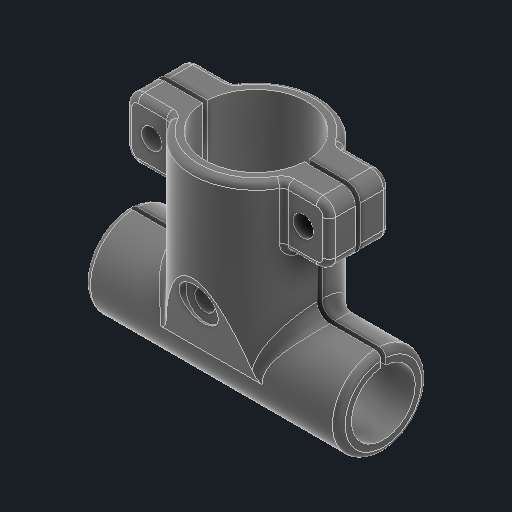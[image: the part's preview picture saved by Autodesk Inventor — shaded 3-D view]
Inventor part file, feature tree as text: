
AUTODESK INVENTOR PART (.ipt)
format: ipt  version: 2024.1 (Build 281209000, 209)  size: 550,400 bytes
history: native  units: mm
features: sketch x11, extrude x10, projected_geometry x7, fillet x4, revolve x2, plane x2
ambient origin geometry x8: Origin, YZ Plane, XZ Plane, XY Plane, X Axis, Y Axis, Z Axis, Center Point
bodies: Solid1 (feature_tree)
feature tree (36):
  sketch  "Sketch1"  dims[d0=40.0mm d1=20.0mm]
  revolve  "Revolution1"  [1 undecoded]
  revolve  "Revolution2"  [1 undecoded]
  extrude  "Extrusion1"  Depth=2.0mm
  extrude  "Extrusion2"  Depth=4.0mm
  extrude  "Extrusion3"  TaperAngle=360.0deg  [1 undecoded]
  extrude  "Extrusion4"  Depth=15.0mm
  extrude  "Extrusion5"  Depth=4.5mm
  plane  "Work Plane1"
  plane  "Work Plane2"
  extrude  "Extrusion6"  Depth=9.5mm
  extrude  "Extrusion7"  Depth=9.5mm
  fillet  "Fillet1"  Radius=9.5mm
  fillet  "Fillet2"  Radius=4.1mm
  fillet  "Fillet3"  Radius=4.1mm
  fillet  "Fillet4"  Radius=3.2mm
  extrude  "Extrusion8"  Depth=9.5mm TaperAngle=0.0deg
  extrude  "Extrusion9"  Depth=10.0mm
  extrude  "Extrusion11"  Depth=10.0mm TaperAngle=0.0deg
  sketch  "Sketch2"  dims[d2=27.0mm d3=6.0mm]
  projected_geometry  "Projected Loop1"
  projected_geometry  "Projected Loop2"
  sketch  "Sketch3"  dims[d4=40.0mm d5=2.0mm]
  sketch  "Sketch4"  dims[d7=8.0mm d8=4.0mm]
  projected_geometry  "Projected Loop3"
  projected_geometry  "Projected Loop4"
  sketch  "Sketch5"  dims[d9=27.0mm d10=360.0deg]
  projected_geometry  "Projected Loop5"
  projected_geometry  "Projected Loop6"
  sketch  "Sketch6"  dims[d11=90.0deg d12=15.0mm]
  projected_geometry  "Projected Loop7"
  sketch  "Sketch7"  dims[d13=23.0mm d14=0.0mm d15=4.5mm]
  sketch  "Sketch8"  dims[d16=16.0mm d17=9.5mm]
  sketch  "Sketch9"  dims[d18=32.0mm d19=9.5mm d20=9.5mm d21=0.0mm d22=4.1mm d23=4.1mm d24=3.2mm]
  sketch  "Sketch10"  dims[d25=3.2mm d26=9.5mm d27=0.0mm]
  sketch  "Sketch12"  dims[d28=3.2mm d29=3.2mm d30=2.0mm d31=0.0mm d32=8.0mm d33=3.2mm d34=0.0mm d35=0.0mm d36=10.0mm d37=-10.0mm d38=6.0mm d39=2.0mm d40=0.0mm d42=2.0mm d43=0.0mm d44=2.0mm d45=2.0mm d46=1.0mm d47=1.0mm d48=27.0mm d49=0.75mm d50=27.0mm d51=10.0mm d52=0.0mm d53=0.0mm d54=3.2mm d55=16.0mm d56=15.0mm d57=0.0mm d61=6.0mm d62=12.25mm d63=0.0mm]
note: 3 required parameter values undecoded (feature->parameter linkage not recoverable at this tier; creation-order binding heuristic only, values carry confidence <= 0.55)